# Revit family: SCST
name_source: partatom
category: Lighting Fixtures
revit_build: Autodesk Revit 2014 (Build: 20130308_1515(x64)
units: mm (PartAtom-declared; Revit-internal decimal feet)

## types (1)
- SCST
    Apparent Load = 0 VA
    Backbox = White
    Color Filter = 16777215
    Default Elevation = 48"
    Description = LENSED STRIPLIGHT WITH SPECTRACLEAN™ ANTIMICROBIAL LIGHTING
    Dimming Lamp Color Temperature Shift = <None>
    Emit Shape Visible in Rendering = No
    Emit from Rectangle Length = 47 1/2"
    Emit from Rectangle Width = 4 1/4"
    Glass = White Glass
    Lamp = LED Lamp
    Manufacturer = Hubbell Lighting
    Model = SCST
    Nominal Watts = 96 W
    Photometric Web File = generic.ies
    Product Documentation Link = https://hubbellcdn.com
    Product Page Link = https://www.hubbell.com
    Row Length = 48"
    Tilt Angle = -90.00°
    URL = https://www.hubbell.com
    Voltage = 120 V
    Warranty = 5 Year Limited Warranty
    Wattage Comments = Up to 110 lumens per watt

## geometry (parser evidence)
native form markers: Sweep x2
no freeform markers — native parametric forms only
